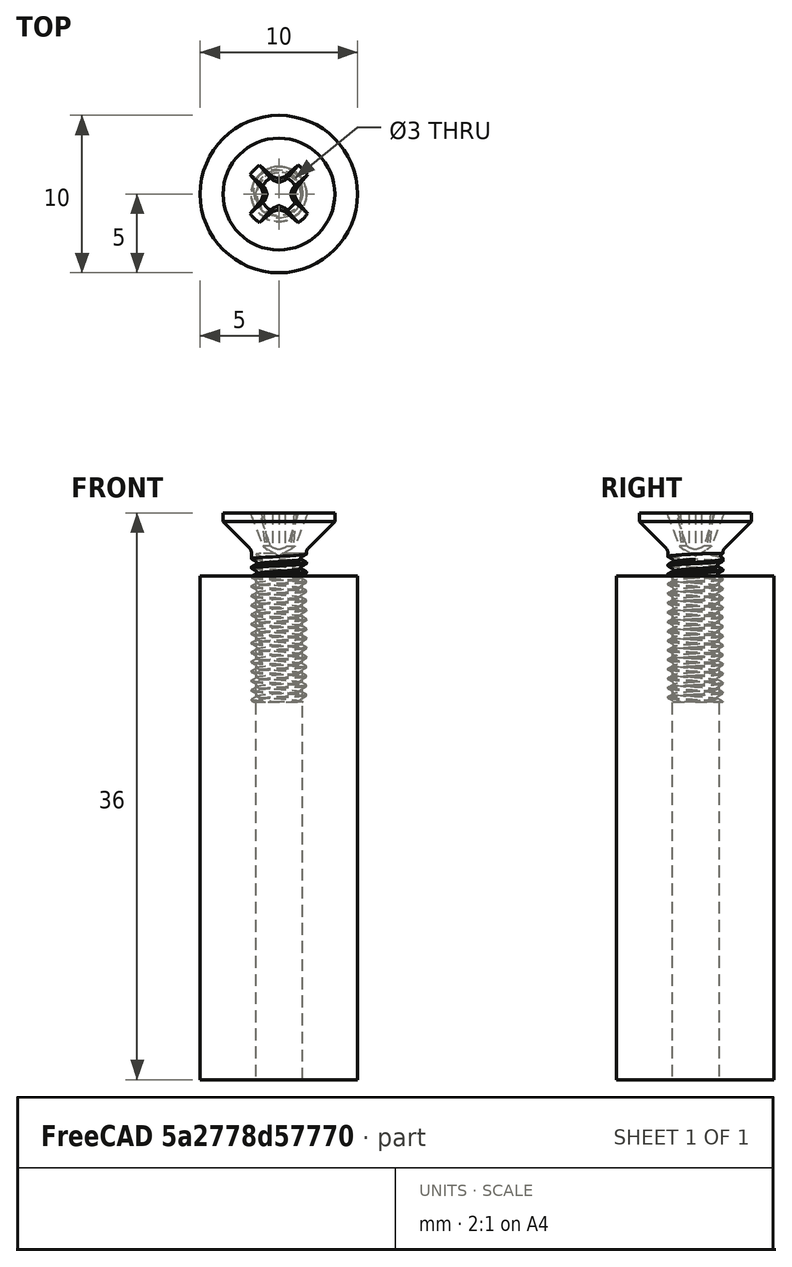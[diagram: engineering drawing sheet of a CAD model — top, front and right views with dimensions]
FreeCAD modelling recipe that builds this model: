
FCSTD DOCUMENT  (FreeCAD 0.21R33771 (Git))
Label: Base-Pin
License: All rights reserved
LicenseURL: http://en.wikipedia.org/wiki/All_rights_reserved
objects: Sketcher::SketchObject×1, PartDesign::Pad×1, PartDesign::Body×1, Part::FeaturePython×1
note: 5 computed .brp shape members not serialized (recipe doc carries the construction recipe); baked Part::Feature solids carry a one-line shape summary decoded from their .brp

FEATURE [Sketcher::SketchObject] Sketch
  FullyConstrained = true
  MapMode = 5
  Support = -> [XY_Plane]
  sketch-geometry (2):
    g0: Circle CenterX=0 CenterY=0 CenterZ=0 NormalX=0 NormalY=0 NormalZ=1 AngleXU=0 Radius=5
    g1: Circle CenterX=0 CenterY=0 CenterZ=0 NormalX=0 NormalY=0 NormalZ=1 AngleXU=0 Radius=1.5
  constraints (4):
    c: Coincident(g0,g-1)
    c: Diameter(g0) = 10
    c: Coincident(g1,g0)
    c: Diameter(g1) = 3
FEATURE [PartDesign::Pad] Pad
  Direction = (0,0,1)
  Length = 32
  Length2 = 10
  Profile = -> Sketch
  ReferenceAxis = -> Sketch [N_Axis]
  Type = 0
FEATURE [PartDesign::Body] Body
  Group = -> [Sketch,Pad]
  Origin = -> Origin
  Tip = -> Pad
FEATURE [Part::FeaturePython] Screw  label="(M3.5)x12-Screw"  # Fasteners workbench fastener (typed FeaturePython)
  Placement = pos=(0,0,36) rot=(0,0,1;0rad)
  baseObject = -> Body
  diameter = 5
  invert = false
  leftHanded = false
  length = 4
  lengthCustom = 12
  matchOuter = false
  offset = 0
  thread = true
  type = 50
